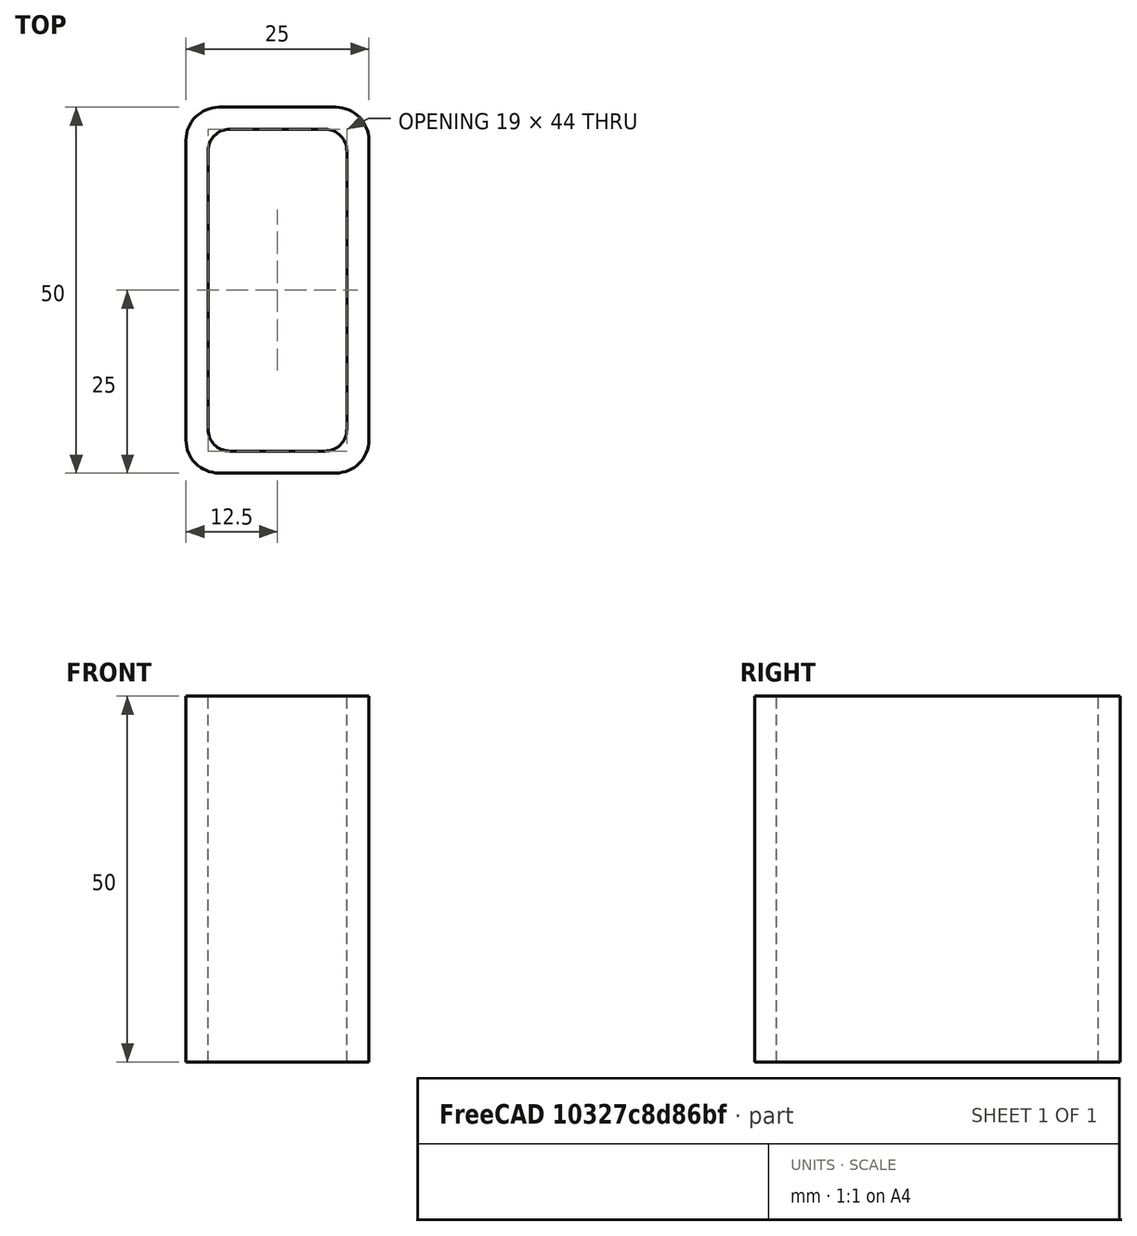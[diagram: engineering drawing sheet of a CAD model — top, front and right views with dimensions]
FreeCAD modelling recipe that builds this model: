
FCSTD DOCUMENT  (FreeCAD 0.15R4671 (Git))
Label: Rectangular hollow section 50x25x3 EN10219 S235JRH
License: All rights reserved
LicenseURL: http://en.wikipedia.org/wiki/All_rights_reserved
objects: Sketcher::SketchObject×1, Part::Extrusion×1
note: 2 computed .brp shape members not serialized (recipe doc carries the construction recipe); baked Part::Feature solids carry a one-line shape summary decoded from their .brp

FEATURE [Sketcher::SketchObject] Sketch
  sketch-geometry (16):
    g0: LineSegment StartX=-6.5 StartY=22 StartZ=0 EndX=6.5 EndY=22 EndZ=0
    g1: LineSegment StartX=9.5 StartY=19 StartZ=0 EndX=9.5 EndY=-19 EndZ=0
    g2: LineSegment StartX=6.5 StartY=-22 StartZ=0 EndX=-6.5 EndY=-22 EndZ=0
    g3: LineSegment StartX=-9.5 StartY=-19 StartZ=0 EndX=-9.5 EndY=19 EndZ=0
    g4: LineSegment StartX=-8 StartY=25 StartZ=0 EndX=8 EndY=25 EndZ=0
    g5: LineSegment StartX=12.5 StartY=20.5 StartZ=0 EndX=12.5 EndY=-20.5 EndZ=0
    g6: LineSegment StartX=8 StartY=-25 StartZ=0 EndX=-8 EndY=-25 EndZ=0
    g7: LineSegment StartX=-12.5 StartY=-20.5 StartZ=0 EndX=-12.5 EndY=20.5 EndZ=0
    g8: ArcOfCircle CenterX=-6.5 CenterY=19 CenterZ=0 NormalX=0 NormalY=0 NormalZ=1 Radius=3 StartAngle=1.5708 EndAngle=3.14159
    g9: ArcOfCircle CenterX=6.5 CenterY=19 CenterZ=0 NormalX=0 NormalY=0 NormalZ=1 Radius=3 StartAngle=0 EndAngle=1.5708
    g10: ArcOfCircle CenterX=6.5 CenterY=-19 CenterZ=0 NormalX=0 NormalY=0 NormalZ=1 Radius=3 StartAngle=4.71239 EndAngle=6.28319
    g11: ArcOfCircle CenterX=-6.5 CenterY=-19 CenterZ=0 NormalX=0 NormalY=0 NormalZ=1 Radius=3 StartAngle=3.14159 EndAngle=4.71239
    g12: ArcOfCircle CenterX=8 CenterY=20.5 CenterZ=0 NormalX=0 NormalY=0 NormalZ=1 Radius=4.5 StartAngle=0 EndAngle=1.5708
    g13: ArcOfCircle CenterX=8 CenterY=-20.5 CenterZ=0 NormalX=0 NormalY=0 NormalZ=1 Radius=4.5 StartAngle=4.71239 EndAngle=6.28319
    g14: ArcOfCircle CenterX=-8 CenterY=-20.5 CenterZ=0 NormalX=0 NormalY=0 NormalZ=1 Radius=4.5 StartAngle=3.14159 EndAngle=4.71239
    g15: ArcOfCircle CenterX=-8 CenterY=20.5 CenterZ=0 NormalX=0 NormalY=0 NormalZ=1 Radius=4.5 StartAngle=1.5708 EndAngle=3.14159
  constraints (36):
    c: Horizontal(g2)
    c: Vertical(g3)
    c: Horizontal(g6)
    c: Vertical(g7)
    c: Tangent(g3,g8) = 1.5708
    c: Tangent(g0,g8) = 1.5708
    c: Tangent(g0,g9) = 1.5708
    c: Tangent(g1,g9) = 1.5708
    c: Tangent(g1,g10) = 1.5708
    c: Tangent(g2,g10) = 1.5708
    c: Tangent(g2,g11) = 1.5708
    c: Tangent(g3,g11) = 1.5708
    c: Tangent(g4,g12) = 1.5708
    c: Tangent(g5,g12) = 1.5708
    c: Tangent(g5,g13) = 1.5708
    c: Tangent(g6,g13) = 1.5708
    c: Tangent(g6,g14) = 1.5708
    c: Tangent(g7,g14) = 1.5708
    c: Tangent(g7,g15) = 1.5708
    c: Tangent(g4,g15) = 1.5708
    c: Equal(g9,g8)
    c: Equal(g9,g11)
    c: Equal(g9,g10)
    c: Equal(g12,g15)
    c: Equal(g12,g14)
    c: Equal(g12,g13)
    c: Symmetric(g4,g6,g-1)
    c: Symmetric(g7,g5,g-2)
    c: DistanceY(g4,g6) = -50
    c: DistanceX(g7,g5) = 25
    c: Symmetric(g3,g1,g-2)
    c: Symmetric(g0,g2,g-1)
    c: DistanceY(g0,g4) = 3
    c: DistanceX(g5,g1) = -3
    c: Radius(g9) = 3
    c: Radius(g12) = 4.5
FEATURE [Part::Extrusion] Extrude  label="Rectangular hollow section 50x25x3 EN10219 S235JRH"
  Base = -> Sketch
  Dir = (0,0,50)
  Solid = true
